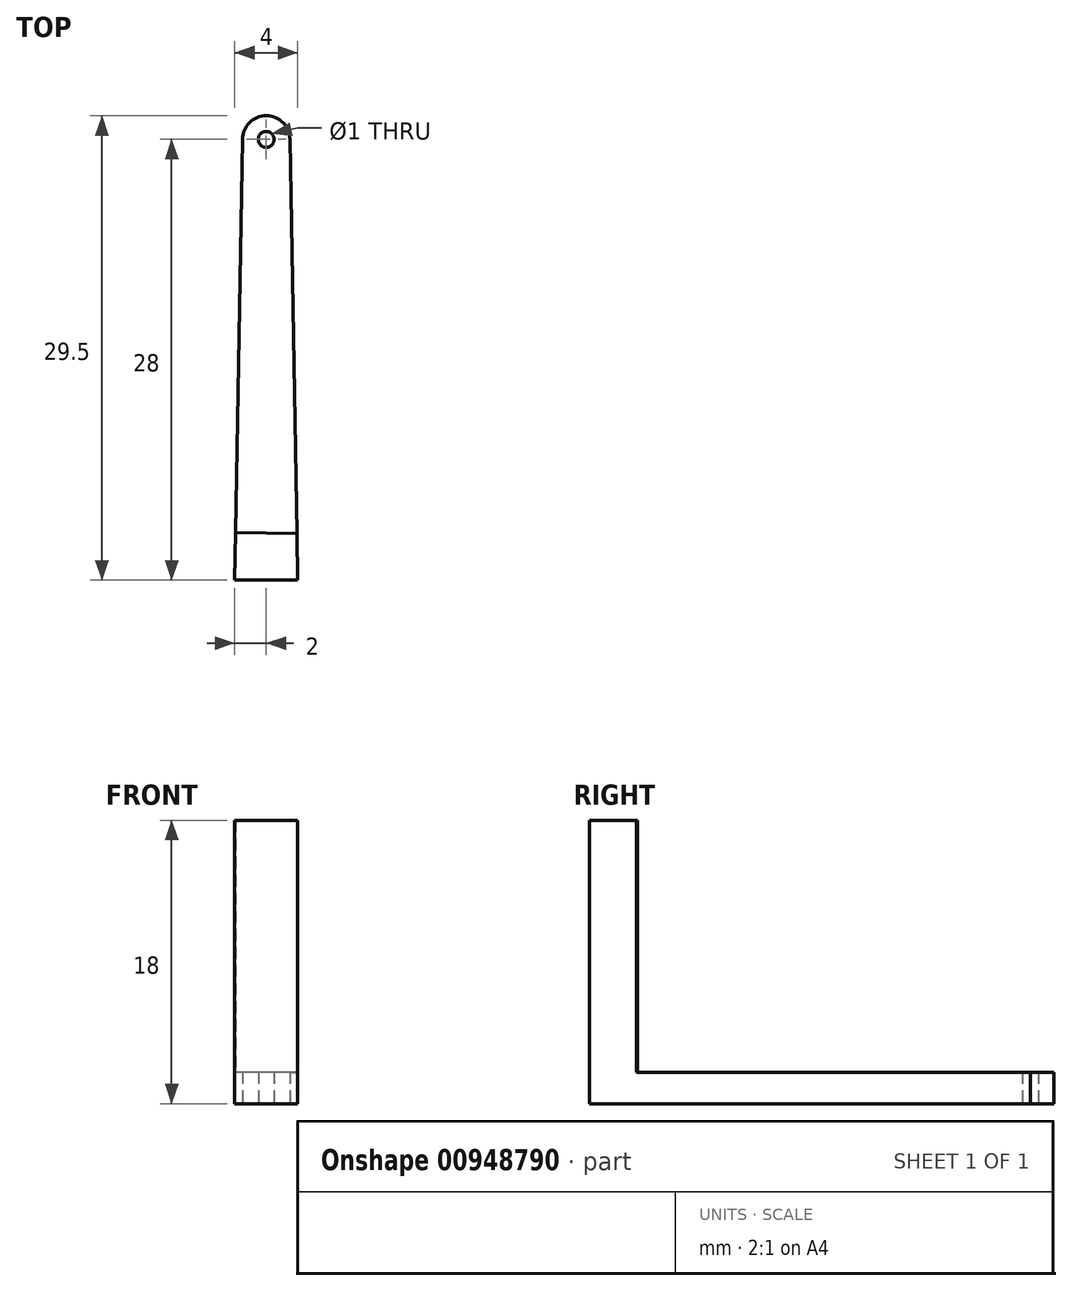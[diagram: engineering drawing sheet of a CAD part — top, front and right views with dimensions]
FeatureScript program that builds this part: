
annotation { "Feature Type Name" : "Feature", "Feature Type Description" : "" }
export const myFeature = defineFeature(function(context is Context, id is Id, definition is map)
    precondition{}
    {
        {
            var Q0;
            Q0=qCreatedBy(makeId("Top.planeOp"),FACE);
            var sketch = newSketch(context, id + "F0", { "sketchPlane" : qUnion([Q0])});
            skLineSegment(sketch, "E0", {"start": v(0, 0) * mm, "end": v(0, 28) * mm});
            skCircle(sketch, "E1", {"center": v(0, 28) * mm, "radius": 0.5 * mm});
            skCircle(sketch, "E2", {"center": v(0, 28) * mm, "radius": 1.5 * mm});
            skLineSegment(sketch, "E3", {"start": v(0, 0) * mm, "end": v(2, 0) * mm});
            skLineSegment(sketch, "E4", {"start": v(0, 0) * mm, "end": v(-2, 0) * mm});
            skPoint(sketch, "E5", {"position": v(-1.5, 28) * mm});
            skPoint(sketch, "E6", {"position": v(1.5, 28) * mm});
            skLineSegment(sketch, "E7", {"start": v(-1.5, 28) * mm, "end": v(-2, 0) * mm});
            skLineSegment(sketch, "E8", {"start": v(1.5, 28) * mm, "end": v(2, 0) * mm});
            skPoint(sketch, "E9", {"position": v(0, 3) * mm});
            skLineSegment(sketch, "E10", {"start": v(0, 3) * mm, "end": v(1.95, 2.97) * mm});
            skLineSegment(sketch, "E11", {"start": v(0, 3) * mm, "end": v(-1.95, 3.03) * mm});
            skSolve(sketch);
        }
        {
            var Q0;
            {var subQ0=sQuery(id+"F0.wireOp",EDGE,"E11");Q0=makeQuery(id+"F0.imprint","IMPRINT",FACE,{"disambiguationData":[TD([[makeQuery(id+"F0.imprint","IMPRINT",EDGE,{"derivedFrom":subQ0}),-1.0]])]});}
            var Q1;
            {var subQ0=sQuery(id+"F0.wireOp",EDGE,"E10");Q1=makeQuery(id+"F0.imprint","IMPRINT",FACE,{"disambiguationData":[TD([[makeQuery(id+"F0.imprint","IMPRINT",EDGE,{"derivedFrom":subQ0}),1.0]])]});}
            var Q2;
            Q2=makeQuery(id+"F0.imprint","IMPRINT",FACE,{"disambiguationData":[TD([[makeQuery(id+"F0.imprint","IMPRINT",EDGE,{"derivedFrom":sQuery(id+"F0.wireOp",EDGE,"E1")}),-1.0]])]});
            extrude(context, id + "F1", {"entities" : qUnion([Q0, Q1, Q2]), "depth" : 2 * mm, "offsetDistance" : 25 * mm});
        }
        {
            var Q0;
            {var subQ0=sQuery(id+"F0.wireOp",EDGE,"E3");Q0=makeQuery(id+"F0.imprint","IMPRINT",FACE,{"disambiguationData":[TD([[makeQuery(id+"F0.imprint","IMPRINT",EDGE,{"derivedFrom":subQ0}),1.0]])]});}
            var Q1;
            {var subQ0=sQuery(id+"F0.wireOp",EDGE,"E4");Q1=makeQuery(id+"F0.imprint","IMPRINT",FACE,{"disambiguationData":[TD([[makeQuery(id+"F0.imprint","IMPRINT",EDGE,{"derivedFrom":subQ0}),-1.0]])]});}
            extrude(context, id + "F2", {"entities" : qUnion([Q0, Q1]), "operationType" : NewBodyOperationType.ADD, "depth" : 18 * mm, "offsetDistance" : 25 * mm});
        }
    });
